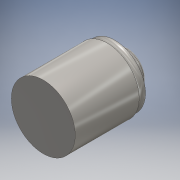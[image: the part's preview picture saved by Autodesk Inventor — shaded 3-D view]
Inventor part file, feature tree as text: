
AUTODESK INVENTOR PART (.ipt)
format: ipt  version: 2016 (Build 200138000, 138)  size: 204,800 bytes
history: native  units: mm
features: sketch x10, extrude x5, plane x4, fillet x4, loft x3, other x2
ambient origin geometry x8: Origin, YZ Plane, XZ Plane, XY Plane, X Axis, Y Axis, Z Axis, Center Point
bodies: Solid1 (feature_tree)
feature tree (28):
  extrude  "Extrusion1"  Depth=58.0mm
  plane  "Work Plane1"
  sketch  "Sketch2"  dims[d2=0.0mm d3=7.0mm]
  plane  "Work Plane2"
  loft  "Loft1"
  plane  "Work Plane4"
  loft  "Loft2"
  loft  "Loft3"
  fillet  "Fillet1"  [1 undecoded]
  extrude  "Extrusion2"  Depth=12.0mm
  fillet  "Fillet2"  Radius=30.0mm
  extrude  "Extrusion3"  TaperAngle=0.0deg  [1 undecoded]
  fillet  "Fillet3"  Radius=32.5mm
  extrude  "Extrusion4"  TaperAngle=0.0deg  [1 undecoded]
  fillet  "Fillet4"  [1 undecoded]
  extrude  "Extrusion5"  Depth=2.0mm
  sketch  "Sketch1"  dims[d0=58.0mm d1=58.0mm]
  sketch  "Sketch3"  dims[d4=55.5mm d5=3.5mm]
  other  "Edges1"
  plane  "Work Plane3"
  sketch  "Sketch4"  dims[d6=53.5mm d7=0.0mm d8=90.0deg d9=0.0mm d10=90.0deg]
  other  "Edges2"
  sketch  "Sketch5"  dims[d11=0.0mm d12=90.0deg d13=12.0mm d14=-4.5mm d15=30.0mm]
  sketch  "Sketch6"  dims[d16=0.0mm d17=90.0deg d18=0.0mm d19=90.0deg d20=32.5mm]
  sketch  "Sketch7"  dims[d21=32.5mm d22=0.0mm d23=90.0deg d24=0.0mm d25=90.0deg]
  sketch  "Sketch8"  dims[d26=2.0mm d27=24.0mm]
  sketch  "Sketch9"  dims[d28=8.0mm d29=0.0mm]
  sketch  "Sketch10"  dims[d30=2.0mm d31=10.5mm d32=8.0mm d33=0.0mm d34=1.0mm d35=4.0mm d36=7.7mm d37=0.0mm d38=0.5mm d39=7.7mm d40=0.0mm]
note: 4 required parameter values undecoded (feature->parameter linkage not recoverable at this tier; creation-order binding heuristic only, values carry confidence <= 0.55)
